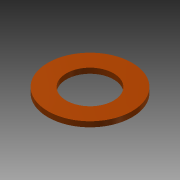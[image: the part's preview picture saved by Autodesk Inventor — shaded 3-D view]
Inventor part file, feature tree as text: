
AUTODESK INVENTOR PART (.ipt)
format: ipt  version: 2013 (Build 170138000, 138)  size: 73,728 bytes
history: native  units: mm
features: extrude x1, sketch x1
ambient origin geometry x8: Origin, YZ Plane, XZ Plane, XY Plane, X Axis, Y Axis, Z Axis, Center Point
bodies: Solid1 (feature_tree)
feature tree (2):
  extrude  "Extrusion1"  Depth=16.0mm
  sketch  "Sketch1"  dims[d0=9.0mm d2=16.0mm d3=1.0mm d4=0.0mm]
